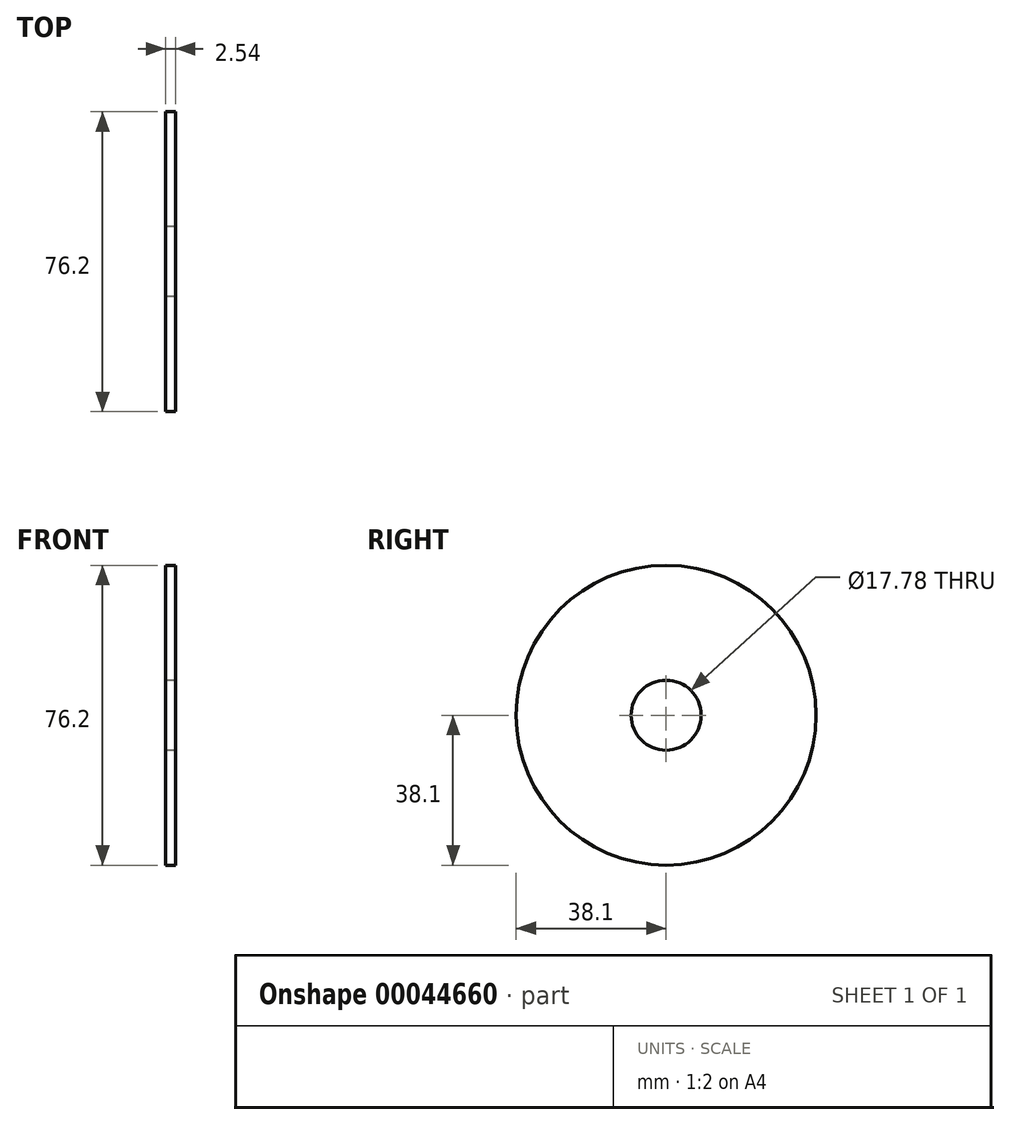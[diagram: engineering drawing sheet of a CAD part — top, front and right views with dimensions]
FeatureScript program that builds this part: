
annotation { "Feature Type Name" : "Feature", "Feature Type Description" : "" }
export const myFeature = defineFeature(function(context is Context, id is Id, definition is map)
    precondition{}
    {
        {
            var Q0;
            Q0=qCreatedBy(makeId("Right.planeOp"),FACE);
            var sketch = newSketch(context, id + "F0", { "sketchPlane" : qUnion([Q0])});
            skCircle(sketch, "E0", {"center": v(0, 0) * mm, "radius": 38.1 * mm});
            skSolve(sketch);
        }
        {
            var Q0;
            Q0=makeQuery(id+"F0.imprint","IMPRINT",FACE,{"disambiguationData":[TD([[makeQuery(id+"F0.imprint","IMPRINT",EDGE,{"derivedFrom":sQuery(id+"F0.wireOp",EDGE,"E0")}),1.0]])]});
            extrude(context, id + "F1", {"entities" : qUnion([Q0]), "depth" : 2.54 * mm});
        }
        {
            var Q0;
            Q0=qCreatedBy(makeId("Right.planeOp"),FACE);
            var sketch = newSketch(context, id + "F2", { "sketchPlane" : qUnion([Q0])});
            skPoint(sketch, "E1", {"position": v(0, 0) * mm});
            skSolve(sketch);
        }
        {
            var Q0;
            Q0=sQuery(id+"F2.wireOp",VERTEX,"E1");
            var Q1;
            Q1=makeQuery(id+"F1.opExtrude","SWEPT_BODY",BODY,{"disambiguationData":[OSD([sQuery(id+"F0.wireOp",EDGE,"E0")])]});
            hole(context, id + "F3", {"style" : HoleStyle.SIMPLE, "holeDiameter" : 17.78 * mm, "endStyle" : HoleEndStyle.THROUGH, "oppositeDirection" : true, "locations" : qUnion([Q0]), "scope" : qUnion([Q1])});
        }
    });
